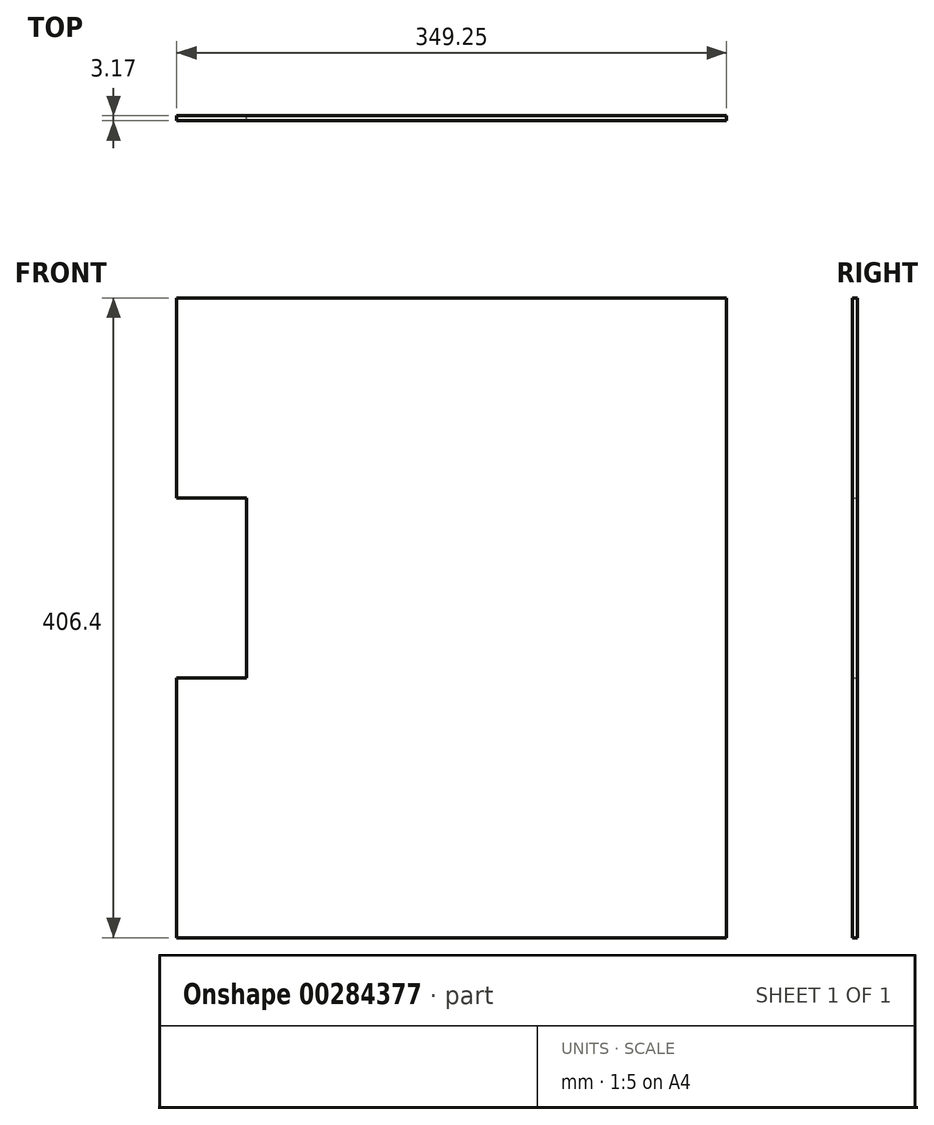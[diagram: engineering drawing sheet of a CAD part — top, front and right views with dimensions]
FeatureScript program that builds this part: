
annotation { "Feature Type Name" : "Feature", "Feature Type Description" : "" }
export const myFeature = defineFeature(function(context is Context, id is Id, definition is map)
    precondition{}
    {
        {
            var Q0;
            Q0=qCreatedBy(makeId("Front.planeOp"),FACE);
            var sketch = newSketch(context, id + "F0", { "sketchPlane" : qUnion([Q0])});
            skLineSegment(sketch, "E0", {"start": v(0, 0) * mm, "end": v(0, 165.1) * mm});
            skLineSegment(sketch, "E1", {"start": v(0, 165.1) * mm, "end": v(44.45, 165.1) * mm});
            skLineSegment(sketch, "E2", {"start": v(44.45, 165.1) * mm, "end": v(44.45, 279.4) * mm});
            skLineSegment(sketch, "E3", {"start": v(44.45, 279.4) * mm, "end": v(0, 279.4) * mm});
            skLineSegment(sketch, "E4", {"start": v(0, 279.4) * mm, "end": v(0, 406.4) * mm});
            skLineSegment(sketch, "E5", {"start": v(0, 406.4) * mm, "end": v(349.25, 406.4) * mm});
            skLineSegment(sketch, "E6", {"start": v(349.25, 406.4) * mm, "end": v(349.25, 0) * mm});
            skLineSegment(sketch, "E7", {"start": v(349.25, 0) * mm, "end": v(0, 0) * mm});
            skSolve(sketch);
        }
        {
            var Q0;
            Q0 = qSketchRegion(id + "F0", true);
            extrude(context, id + "F1", {"entities" : qUnion([Q0]), "depth" : 3.17 * mm});
        }
    });
